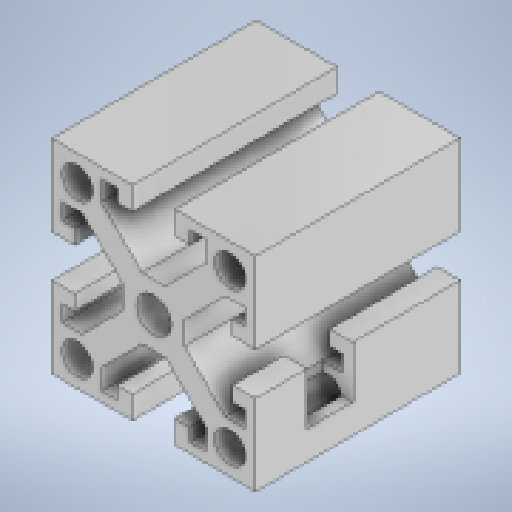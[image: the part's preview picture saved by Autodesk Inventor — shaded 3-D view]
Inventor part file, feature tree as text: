
AUTODESK INVENTOR PART (.ipt)
format: ipt  version: 2024.1 (Build 281209000, 209)  size: 336,896 bytes
history: native  units: in
note: dims shown in document units (in); Inventor stores cm internally (conversion verified against a paired STEP export)
features: reference x4, extrude x2, sketch x2, other x2
ambient origin geometry x8: Origin, YZ Plane, XZ Plane, XY Plane, X Axis, Y Axis, Z Axis, Center Point
bodies: Solid1 (feature_tree)
feature tree (10):
  extrude  "Extrusion1"  TaperAngle=45.0deg  [1 undecoded]
  extrude  "Extrusion2"  Depth=0.2362in
  sketch  "Sketch1"  dims[d0=0.2677in d1=45.0deg]
  sketch  "Sketch2"  dims[d2=0.7874in d3=0.2362in d4=0.5906in d5=0.4035in d6=0.2795in d7=0.1634in d8=0.1772in d9=0.0787in d10=0.5492in d11=0.2362in d12=1.5748in d14=360.0deg d16=1.5787in d17=0.0in d18=0.0108in d19=0.2362in d20=0.0in]
  reference  "Reference1"
  reference  "Reference2"
  reference  "Reference3"
  reference  "Reference4"
  other  "1_Base.iam"
  other  "HTD-45H:1"
note: 1 required parameter value undecoded (feature->parameter linkage not recoverable at this tier; creation-order binding heuristic only, values carry confidence <= 0.55)
